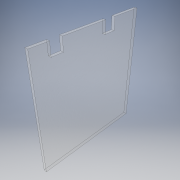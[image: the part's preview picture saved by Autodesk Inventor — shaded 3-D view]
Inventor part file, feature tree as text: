
AUTODESK INVENTOR PART (.ipt)
format: ipt  version: 2019 (Build 230136000, 136)  size: 118,784 bytes
history: native  units: in
note: dims shown in document units (in); Inventor stores cm internally (conversion verified against a paired STEP export)
features: extrude x2, sketch x2, projected_geometry x1
ambient origin geometry x8: Origin, YZ Plane, XZ Plane, XY Plane, X Axis, Y Axis, Z Axis, Center Point
bodies: Solid1 (feature_tree)
feature tree (5):
  extrude  "Extrusion1"  Depth=7.5in
  extrude  "Extrusion2"  Depth=4.4062in
  sketch  "Sketch1"  dims[d0=8.0in d1=7.5in]
  sketch  "Sketch2"  dims[d2=0.21in d3=0.0in d4=4.4062in d5=2.9375in d6=0.8125in d7=1.5in d8=0.21in d9=0.0in]
  projected_geometry  "Projected Loop1"
